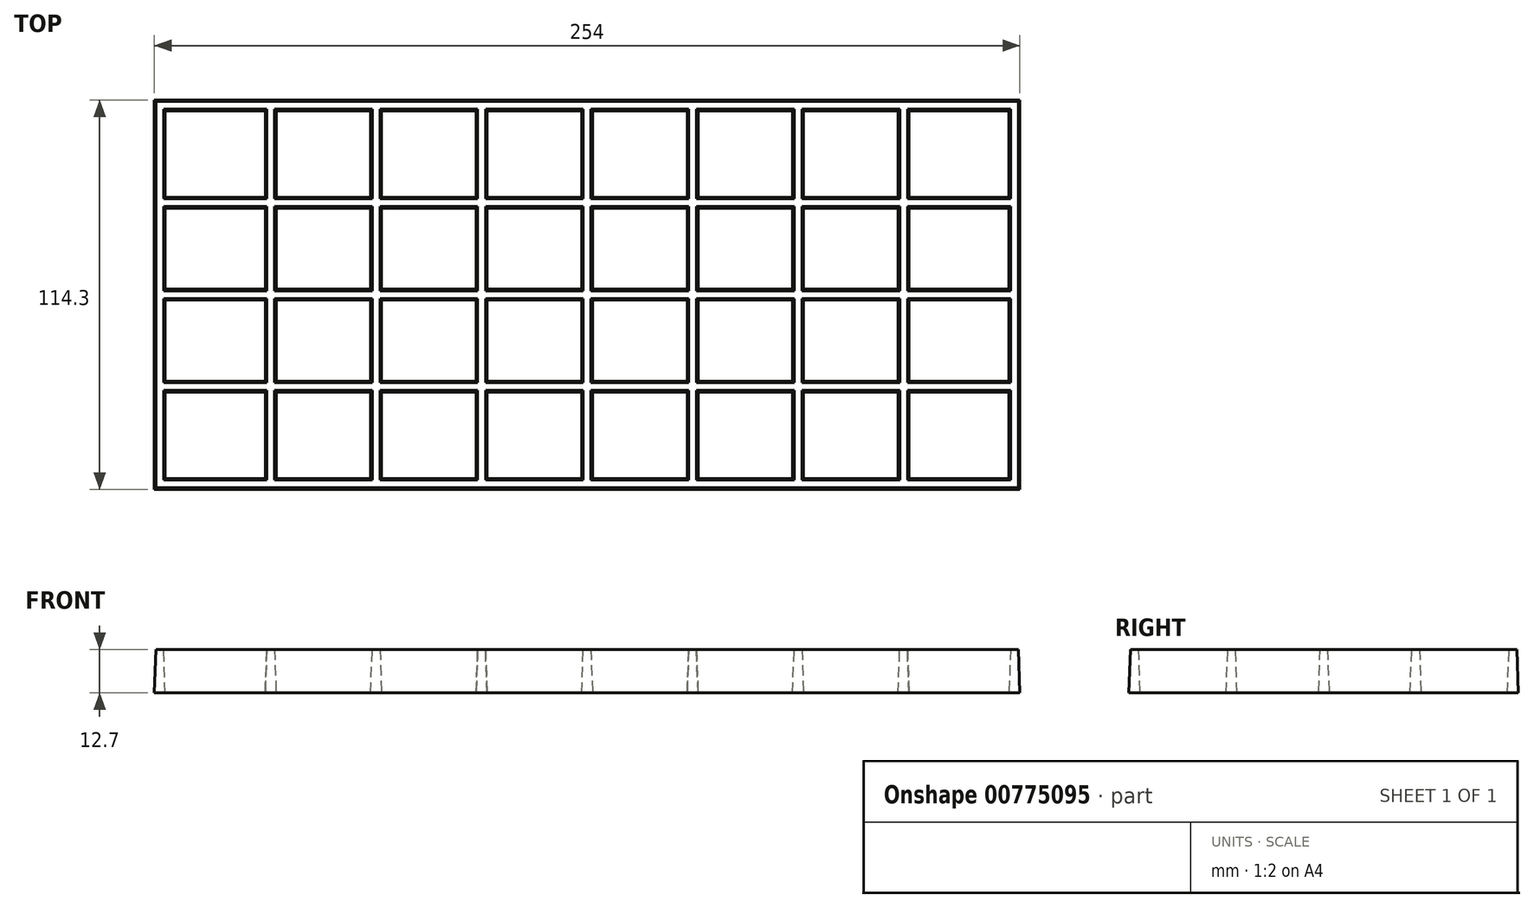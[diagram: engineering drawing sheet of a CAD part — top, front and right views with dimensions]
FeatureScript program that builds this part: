
annotation { "Feature Type Name" : "Feature", "Feature Type Description" : "" }
export const myFeature = defineFeature(function(context is Context, id is Id, definition is map)
    precondition{}
    {
        {
            var Q0;
            Q0=qCreatedBy(makeId("Top.planeOp"),FACE);
            var sketch = newSketch(context, id + "F0", { "sketchPlane" : qUnion([Q0])});
            skLineSegment(sketch, "E0.bottom", {"start": v(127, 57.15) * mm, "end": v(-127, 57.15) * mm});
            skLineSegment(sketch, "E0.top", {"start": v(127, -57.15) * mm, "end": v(-127, -57.15) * mm});
            skLineSegment(sketch, "E0.left", {"start": v(127, 57.15) * mm, "end": v(127, -57.15) * mm});
            skLineSegment(sketch, "E0.right", {"start": v(-127, 57.15) * mm, "end": v(-127, -57.15) * mm});
            skPoint(sketch, "E0.middle", {"position": v(0, 0) * mm});
            skLineSegment(sketch, "E1.0", {"start": v(123.82, 53.97) * mm, "end": v(-123.83, 53.98) * mm});
            skLineSegment(sketch, "E1.1", {"start": v(123.82, 53.97) * mm, "end": v(123.82, -53.97) * mm});
            skLineSegment(sketch, "E1.2", {"start": v(123.82, -53.98) * mm, "end": v(-123.83, -53.98) * mm});
            skLineSegment(sketch, "E1.3", {"start": v(-123.82, 53.98) * mm, "end": v(-123.83, -53.98) * mm});
            skLineSegment(sketch, "E2", {"start": v(-123.82, 26.99) * mm, "end": v(123.82, 26.99) * mm, "construction": true});
            skLineSegment(sketch, "E3", {"start": v(-123.83, 0) * mm, "end": v(123.82, 0) * mm, "construction": true});
            skLineSegment(sketch, "E4", {"start": v(-123.83, -26.99) * mm, "end": v(123.82, -26.99) * mm, "construction": true});
            skLineSegment(sketch, "E5", {"start": v(-92.87, 53.98) * mm, "end": v(-92.87, -53.98) * mm, "construction": true});
            skLineSegment(sketch, "E6", {"start": v(-61.91, 53.98) * mm, "end": v(-61.91, -53.98) * mm, "construction": true});
            skLineSegment(sketch, "E7", {"start": v(-30.96, 53.98) * mm, "end": v(-30.96, -53.98) * mm, "construction": true});
            skLineSegment(sketch, "E8", {"start": v(0, 53.98) * mm, "end": v(0, -53.98) * mm, "construction": true});
            skLineSegment(sketch, "E9", {"start": v(30.96, 53.98) * mm, "end": v(30.96, -53.98) * mm, "construction": true});
            skLineSegment(sketch, "E10", {"start": v(61.91, -53.98) * mm, "end": v(61.91, 53.98) * mm, "construction": true});
            skLineSegment(sketch, "E11", {"start": v(92.87, 53.97) * mm, "end": v(92.87, -53.97) * mm, "construction": true});
            skLineSegment(sketch, "E12.bottom", {"start": v(123.82, 28.58) * mm, "end": v(-123.82, 28.58) * mm});
            skLineSegment(sketch, "E12.top", {"start": v(123.82, 25.4) * mm, "end": v(-123.82, 25.4) * mm});
            skLineSegment(sketch, "E12.left", {"start": v(123.82, 28.58) * mm, "end": v(123.82, 25.4) * mm});
            skLineSegment(sketch, "E12.right", {"start": v(-123.82, 28.58) * mm, "end": v(-123.82, 25.4) * mm});
            skPoint(sketch, "E12.middle", {"position": v(0, 26.99) * mm});
            skLineSegment(sketch, "E13.bottom", {"start": v(123.82, 1.59) * mm, "end": v(-123.82, 1.59) * mm});
            skLineSegment(sketch, "E13.top", {"start": v(123.82, -1.59) * mm, "end": v(-123.82, -1.59) * mm});
            skLineSegment(sketch, "E13.left", {"start": v(123.82, 1.59) * mm, "end": v(123.82, -1.59) * mm});
            skLineSegment(sketch, "E13.right", {"start": v(-123.82, 1.59) * mm, "end": v(-123.82, -1.59) * mm});
            skLineSegment(sketch, "E14.bottom", {"start": v(123.82, -25.4) * mm, "end": v(-123.82, -25.4) * mm});
            skLineSegment(sketch, "E14.top", {"start": v(123.82, -28.57) * mm, "end": v(-123.82, -28.57) * mm});
            skLineSegment(sketch, "E14.left", {"start": v(123.82, -25.4) * mm, "end": v(123.82, -28.57) * mm});
            skLineSegment(sketch, "E14.right", {"start": v(-123.83, -25.4) * mm, "end": v(-123.83, -28.57) * mm});
            skPoint(sketch, "E14.middle", {"position": v(0, -26.99) * mm});
            skLineSegment(sketch, "E15.bottom", {"start": v(-91.28, 53.98) * mm, "end": v(-94.46, 53.98) * mm});
            skLineSegment(sketch, "E15.top", {"start": v(-91.28, -53.98) * mm, "end": v(-94.46, -53.98) * mm});
            skLineSegment(sketch, "E15.left", {"start": v(-91.28, 53.98) * mm, "end": v(-91.28, -53.98) * mm});
            skLineSegment(sketch, "E15.right", {"start": v(-94.46, 53.98) * mm, "end": v(-94.46, -53.98) * mm});
            skPoint(sketch, "E15.middle", {"position": v(-92.87, 0) * mm});
            skLineSegment(sketch, "E16.bottom", {"start": v(-60.32, 53.98) * mm, "end": v(-63.5, 53.98) * mm});
            skLineSegment(sketch, "E16.top", {"start": v(-60.32, -53.98) * mm, "end": v(-63.5, -53.98) * mm});
            skLineSegment(sketch, "E16.left", {"start": v(-60.32, 53.98) * mm, "end": v(-60.32, -53.98) * mm});
            skLineSegment(sketch, "E16.right", {"start": v(-63.5, 53.98) * mm, "end": v(-63.5, -53.98) * mm});
            skPoint(sketch, "E16.middle", {"position": v(-61.91, 0) * mm});
            skLineSegment(sketch, "E17.bottom", {"start": v(-29.37, 53.98) * mm, "end": v(-32.54, 53.98) * mm});
            skLineSegment(sketch, "E17.top", {"start": v(-29.37, -53.98) * mm, "end": v(-32.54, -53.98) * mm});
            skLineSegment(sketch, "E17.left", {"start": v(-29.37, 53.98) * mm, "end": v(-29.37, -53.98) * mm});
            skLineSegment(sketch, "E17.right", {"start": v(-32.54, 53.98) * mm, "end": v(-32.54, -53.98) * mm});
            skPoint(sketch, "E17.middle", {"position": v(-30.96, 0) * mm});
            skLineSegment(sketch, "E18.bottom", {"start": v(1.59, 53.98) * mm, "end": v(-1.59, 53.98) * mm});
            skLineSegment(sketch, "E18.top", {"start": v(1.59, -53.98) * mm, "end": v(-1.59, -53.98) * mm});
            skLineSegment(sketch, "E18.left", {"start": v(1.59, 53.98) * mm, "end": v(1.59, -53.98) * mm});
            skLineSegment(sketch, "E18.right", {"start": v(-1.59, 53.98) * mm, "end": v(-1.59, -53.98) * mm});
            skLineSegment(sketch, "E19.bottom", {"start": v(32.54, 53.98) * mm, "end": v(29.37, 53.98) * mm});
            skLineSegment(sketch, "E19.top", {"start": v(32.54, -53.98) * mm, "end": v(29.37, -53.98) * mm});
            skLineSegment(sketch, "E19.left", {"start": v(32.54, 53.98) * mm, "end": v(32.54, -53.98) * mm});
            skLineSegment(sketch, "E19.right", {"start": v(29.37, 53.98) * mm, "end": v(29.37, -53.98) * mm});
            skPoint(sketch, "E19.middle", {"position": v(30.96, 0) * mm});
            skLineSegment(sketch, "E20.bottom", {"start": v(63.5, 53.98) * mm, "end": v(60.33, 53.98) * mm});
            skLineSegment(sketch, "E20.top", {"start": v(63.5, -53.98) * mm, "end": v(60.33, -53.98) * mm});
            skLineSegment(sketch, "E20.left", {"start": v(63.5, 53.98) * mm, "end": v(63.5, -53.98) * mm});
            skLineSegment(sketch, "E20.right", {"start": v(60.33, 53.98) * mm, "end": v(60.33, -53.98) * mm});
            skPoint(sketch, "E20.middle", {"position": v(61.91, 0) * mm});
            skLineSegment(sketch, "E21.bottom", {"start": v(94.46, 53.97) * mm, "end": v(91.28, 53.97) * mm});
            skLineSegment(sketch, "E21.top", {"start": v(94.46, -53.97) * mm, "end": v(91.28, -53.97) * mm});
            skLineSegment(sketch, "E21.left", {"start": v(94.46, 53.98) * mm, "end": v(94.46, -53.98) * mm});
            skLineSegment(sketch, "E21.right", {"start": v(91.28, 53.98) * mm, "end": v(91.28, -53.98) * mm});
            skPoint(sketch, "E21.middle", {"position": v(92.87, 0) * mm});
            skSolve(sketch);
        }
        {
            var Q0;
            Q0=makeQuery(id+"F0.imprint","IMPRINT",FACE,{"disambiguationData":[TD([[makeQuery(id+"F0.imprint","IMPRINT",EDGE,{"derivedFrom":sQuery(id+"F0.wireOp",EDGE,"E0.bottom")}),1.0]])]});
            var Q1;
            {var subQ0=sQuery(id+"F0.wireOp",EDGE,"E15.right");var subQ1=sQuery(id+"F0.wireOp",EDGE,"E1.0");var subQ2=makeQuery(id+"F0.imprint","INTERSECT",VERTEX,{"derivedFrom":[subQ1,subQ0]});Q1=makeQuery(id+"F0.imprint","IMPRINT",FACE,{"disambiguationData":[TD([[makeQuery(id+"F0.imprint","IMPRINT",EDGE,{"disambiguationData":[TD([[subQ2,1.0]])],"derivedFrom":subQ1}),1.0]])]});}
            var Q2;
            {var subQ0=sQuery(id+"F0.wireOp",EDGE,"E16.right");var subQ1=sQuery(id+"F0.wireOp",EDGE,"E1.0");var subQ2=makeQuery(id+"F0.imprint","INTERSECT",VERTEX,{"derivedFrom":[subQ1,subQ0]});Q2=makeQuery(id+"F0.imprint","IMPRINT",FACE,{"disambiguationData":[TD([[makeQuery(id+"F0.imprint","IMPRINT",EDGE,{"disambiguationData":[TD([[subQ2,1.0]])],"derivedFrom":subQ1}),1.0]])]});}
            var Q3;
            {var subQ0=sQuery(id+"F0.wireOp",EDGE,"E17.right");var subQ1=sQuery(id+"F0.wireOp",EDGE,"E1.0");var subQ2=makeQuery(id+"F0.imprint","INTERSECT",VERTEX,{"derivedFrom":[subQ1,subQ0]});Q3=makeQuery(id+"F0.imprint","IMPRINT",FACE,{"disambiguationData":[TD([[makeQuery(id+"F0.imprint","IMPRINT",EDGE,{"disambiguationData":[TD([[subQ2,1.0]])],"derivedFrom":subQ1}),1.0]])]});}
            var Q4;
            {var subQ0=sQuery(id+"F0.wireOp",EDGE,"E18.left");var subQ1=sQuery(id+"F0.wireOp",EDGE,"E1.0");var subQ2=makeQuery(id+"F0.imprint","INTERSECT",VERTEX,{"derivedFrom":[subQ1,subQ0]});Q4=makeQuery(id+"F0.imprint","IMPRINT",FACE,{"disambiguationData":[TD([[makeQuery(id+"F0.imprint","IMPRINT",EDGE,{"disambiguationData":[TD([[subQ2,-1.0]])],"derivedFrom":subQ1}),1.0]])]});}
            var Q5;
            {var subQ0=sQuery(id+"F0.wireOp",EDGE,"E19.right");var subQ1=sQuery(id+"F0.wireOp",EDGE,"E1.0");var subQ2=makeQuery(id+"F0.imprint","INTERSECT",VERTEX,{"derivedFrom":[subQ1,subQ0]});Q5=makeQuery(id+"F0.imprint","IMPRINT",FACE,{"disambiguationData":[TD([[makeQuery(id+"F0.imprint","IMPRINT",EDGE,{"disambiguationData":[TD([[subQ2,1.0]])],"derivedFrom":subQ1}),1.0]])]});}
            var Q6;
            {var subQ0=sQuery(id+"F0.wireOp",EDGE,"E20.right");var subQ1=sQuery(id+"F0.wireOp",EDGE,"E1.0");var subQ2=makeQuery(id+"F0.imprint","INTERSECT",VERTEX,{"derivedFrom":[subQ1,subQ0]});Q6=makeQuery(id+"F0.imprint","IMPRINT",FACE,{"disambiguationData":[TD([[makeQuery(id+"F0.imprint","IMPRINT",EDGE,{"disambiguationData":[TD([[subQ2,1.0]])],"derivedFrom":subQ1}),1.0]])]});}
            var Q7;
            {var subQ0=sQuery(id+"F0.wireOp",EDGE,"E21.left");var subQ1=sQuery(id+"F0.wireOp",EDGE,"E1.0");var subQ2=makeQuery(id+"F0.imprint","INTERSECT",VERTEX,{"derivedFrom":[subQ1,subQ0]});Q7=makeQuery(id+"F0.imprint","IMPRINT",FACE,{"disambiguationData":[TD([[makeQuery(id+"F0.imprint","IMPRINT",EDGE,{"disambiguationData":[TD([[subQ2,-1.0]])],"derivedFrom":subQ1}),1.0]])]});}
            var Q8;
            {var subQ0=sQuery(id+"F0.wireOp",EDGE,"E12.top");var subQ1=sQuery(id+"F0.wireOp",EDGE,"E1.1");var subQ2=makeQuery(id+"F0.imprint","INTERSECT",VERTEX,{"derivedFrom":[subQ1,subQ0]});Q8=makeQuery(id+"F0.imprint","IMPRINT",FACE,{"disambiguationData":[TD([[makeQuery(id+"F0.imprint","IMPRINT",EDGE,{"disambiguationData":[TD([[subQ2,1.0]])],"derivedFrom":subQ1}),-1.0]])]});}
            var Q9;
            {var subQ0=sQuery(id+"F0.wireOp",EDGE,"E21.left");var subQ1=sQuery(id+"F0.wireOp",EDGE,"E12.bottom");var subQ2=makeQuery(id+"F0.imprint","INTERSECT",VERTEX,{"derivedFrom":[subQ1,subQ0]});Q9=makeQuery(id+"F0.imprint","IMPRINT",FACE,{"disambiguationData":[TD([[makeQuery(id+"F0.imprint","IMPRINT",EDGE,{"disambiguationData":[TD([[subQ2,-1.0]])],"derivedFrom":subQ1}),1.0]])]});}
            var Q10;
            {var subQ0=sQuery(id+"F0.wireOp",EDGE,"E21.right");var subQ1=sQuery(id+"F0.wireOp",EDGE,"E12.bottom");var subQ2=makeQuery(id+"F0.imprint","INTERSECT",VERTEX,{"derivedFrom":[subQ1,subQ0]});Q10=makeQuery(id+"F0.imprint","IMPRINT",FACE,{"disambiguationData":[TD([[makeQuery(id+"F0.imprint","IMPRINT",EDGE,{"disambiguationData":[TD([[subQ2,-1.0]])],"derivedFrom":subQ1}),1.0]])]});}
            var Q11;
            {var subQ0=sQuery(id+"F0.wireOp",EDGE,"E20.left");var subQ1=sQuery(id+"F0.wireOp",EDGE,"E12.bottom");var subQ2=makeQuery(id+"F0.imprint","INTERSECT",VERTEX,{"derivedFrom":[subQ1,subQ0]});Q11=makeQuery(id+"F0.imprint","IMPRINT",FACE,{"disambiguationData":[TD([[makeQuery(id+"F0.imprint","IMPRINT",EDGE,{"disambiguationData":[TD([[subQ2,-1.0]])],"derivedFrom":subQ1}),1.0]])]});}
            var Q12;
            {var subQ0=sQuery(id+"F0.wireOp",EDGE,"E19.right");var subQ1=sQuery(id+"F0.wireOp",EDGE,"E12.bottom");var subQ2=makeQuery(id+"F0.imprint","INTERSECT",VERTEX,{"derivedFrom":[subQ1,subQ0]});Q12=makeQuery(id+"F0.imprint","IMPRINT",FACE,{"disambiguationData":[TD([[makeQuery(id+"F0.imprint","IMPRINT",EDGE,{"disambiguationData":[TD([[subQ2,1.0]])],"derivedFrom":subQ1}),1.0]])]});}
            var Q13;
            {var subQ0=sQuery(id+"F0.wireOp",EDGE,"E19.left");var subQ1=sQuery(id+"F0.wireOp",EDGE,"E12.bottom");var subQ2=makeQuery(id+"F0.imprint","INTERSECT",VERTEX,{"derivedFrom":[subQ1,subQ0]});Q13=makeQuery(id+"F0.imprint","IMPRINT",FACE,{"disambiguationData":[TD([[makeQuery(id+"F0.imprint","IMPRINT",EDGE,{"disambiguationData":[TD([[subQ2,1.0]])],"derivedFrom":subQ1}),1.0]])]});}
            var Q14;
            {var subQ0=sQuery(id+"F0.wireOp",EDGE,"E19.right");var subQ1=sQuery(id+"F0.wireOp",EDGE,"E12.bottom");var subQ2=makeQuery(id+"F0.imprint","INTERSECT",VERTEX,{"derivedFrom":[subQ1,subQ0]});Q14=makeQuery(id+"F0.imprint","IMPRINT",FACE,{"disambiguationData":[TD([[makeQuery(id+"F0.imprint","IMPRINT",EDGE,{"disambiguationData":[TD([[subQ2,-1.0]])],"derivedFrom":subQ1}),1.0]])]});}
            var Q15;
            {var subQ0=sQuery(id+"F0.wireOp",EDGE,"E18.left");var subQ1=sQuery(id+"F0.wireOp",EDGE,"E12.bottom");var subQ2=makeQuery(id+"F0.imprint","INTERSECT",VERTEX,{"derivedFrom":[subQ1,subQ0]});Q15=makeQuery(id+"F0.imprint","IMPRINT",FACE,{"disambiguationData":[TD([[makeQuery(id+"F0.imprint","IMPRINT",EDGE,{"disambiguationData":[TD([[subQ2,-1.0]])],"derivedFrom":subQ1}),1.0]])]});}
            var Q16;
            {var subQ0=sQuery(id+"F0.wireOp",EDGE,"E17.left");var subQ1=sQuery(id+"F0.wireOp",EDGE,"E12.bottom");var subQ2=makeQuery(id+"F0.imprint","INTERSECT",VERTEX,{"derivedFrom":[subQ1,subQ0]});Q16=makeQuery(id+"F0.imprint","IMPRINT",FACE,{"disambiguationData":[TD([[makeQuery(id+"F0.imprint","IMPRINT",EDGE,{"disambiguationData":[TD([[subQ2,1.0]])],"derivedFrom":subQ1}),1.0]])]});}
            var Q17;
            {var subQ0=sQuery(id+"F0.wireOp",EDGE,"E17.right");var subQ1=sQuery(id+"F0.wireOp",EDGE,"E12.bottom");var subQ2=makeQuery(id+"F0.imprint","INTERSECT",VERTEX,{"derivedFrom":[subQ1,subQ0]});Q17=makeQuery(id+"F0.imprint","IMPRINT",FACE,{"disambiguationData":[TD([[makeQuery(id+"F0.imprint","IMPRINT",EDGE,{"disambiguationData":[TD([[subQ2,1.0]])],"derivedFrom":subQ1}),1.0]])]});}
            var Q18;
            {var subQ0=sQuery(id+"F0.wireOp",EDGE,"E17.right");var subQ1=sQuery(id+"F0.wireOp",EDGE,"E12.bottom");var subQ2=makeQuery(id+"F0.imprint","INTERSECT",VERTEX,{"derivedFrom":[subQ1,subQ0]});Q18=makeQuery(id+"F0.imprint","IMPRINT",FACE,{"disambiguationData":[TD([[makeQuery(id+"F0.imprint","IMPRINT",EDGE,{"disambiguationData":[TD([[subQ2,-1.0]])],"derivedFrom":subQ1}),1.0]])]});}
            var Q19;
            {var subQ0=sQuery(id+"F0.wireOp",EDGE,"E16.right");var subQ1=sQuery(id+"F0.wireOp",EDGE,"E12.bottom");var subQ2=makeQuery(id+"F0.imprint","INTERSECT",VERTEX,{"derivedFrom":[subQ1,subQ0]});Q19=makeQuery(id+"F0.imprint","IMPRINT",FACE,{"disambiguationData":[TD([[makeQuery(id+"F0.imprint","IMPRINT",EDGE,{"disambiguationData":[TD([[subQ2,1.0]])],"derivedFrom":subQ1}),1.0]])]});}
            var Q20;
            {var subQ0=sQuery(id+"F0.wireOp",EDGE,"E16.right");var subQ1=sQuery(id+"F0.wireOp",EDGE,"E12.bottom");var subQ2=makeQuery(id+"F0.imprint","INTERSECT",VERTEX,{"derivedFrom":[subQ1,subQ0]});Q20=makeQuery(id+"F0.imprint","IMPRINT",FACE,{"disambiguationData":[TD([[makeQuery(id+"F0.imprint","IMPRINT",EDGE,{"disambiguationData":[TD([[subQ2,-1.0]])],"derivedFrom":subQ1}),1.0]])]});}
            var Q21;
            {var subQ0=sQuery(id+"F0.wireOp",EDGE,"E15.right");var subQ1=sQuery(id+"F0.wireOp",EDGE,"E12.bottom");var subQ2=makeQuery(id+"F0.imprint","INTERSECT",VERTEX,{"derivedFrom":[subQ1,subQ0]});Q21=makeQuery(id+"F0.imprint","IMPRINT",FACE,{"disambiguationData":[TD([[makeQuery(id+"F0.imprint","IMPRINT",EDGE,{"disambiguationData":[TD([[subQ2,1.0]])],"derivedFrom":subQ1}),1.0]])]});}
            var Q22;
            {var subQ0=sQuery(id+"F0.wireOp",EDGE,"E12.top");var subQ1=sQuery(id+"F0.wireOp",EDGE,"E1.3");var subQ2=makeQuery(id+"F0.imprint","INTERSECT",VERTEX,{"derivedFrom":[subQ1,subQ0]});Q22=makeQuery(id+"F0.imprint","IMPRINT",FACE,{"disambiguationData":[TD([[makeQuery(id+"F0.imprint","IMPRINT",EDGE,{"disambiguationData":[TD([[subQ2,1.0]])],"derivedFrom":subQ1}),1.0]])]});}
            var Q23;
            {var subQ0=sQuery(id+"F0.wireOp",EDGE,"E15.right");var subQ1=sQuery(id+"F0.wireOp",EDGE,"E12.top");var subQ2=makeQuery(id+"F0.imprint","INTERSECT",VERTEX,{"derivedFrom":[subQ1,subQ0]});Q23=makeQuery(id+"F0.imprint","IMPRINT",FACE,{"disambiguationData":[TD([[makeQuery(id+"F0.imprint","IMPRINT",EDGE,{"disambiguationData":[TD([[subQ2,1.0]])],"derivedFrom":subQ1}),1.0]])]});}
            var Q24;
            {var subQ0=sQuery(id+"F0.wireOp",EDGE,"E16.left");var subQ1=sQuery(id+"F0.wireOp",EDGE,"E12.top");var subQ2=makeQuery(id+"F0.imprint","INTERSECT",VERTEX,{"derivedFrom":[subQ1,subQ0]});Q24=makeQuery(id+"F0.imprint","IMPRINT",FACE,{"disambiguationData":[TD([[makeQuery(id+"F0.imprint","IMPRINT",EDGE,{"disambiguationData":[TD([[subQ2,-1.0]])],"derivedFrom":subQ1}),1.0]])]});}
            var Q25;
            {var subQ0=sQuery(id+"F0.wireOp",EDGE,"E17.right");var subQ1=sQuery(id+"F0.wireOp",EDGE,"E12.top");var subQ2=makeQuery(id+"F0.imprint","INTERSECT",VERTEX,{"derivedFrom":[subQ1,subQ0]});Q25=makeQuery(id+"F0.imprint","IMPRINT",FACE,{"disambiguationData":[TD([[makeQuery(id+"F0.imprint","IMPRINT",EDGE,{"disambiguationData":[TD([[subQ2,1.0]])],"derivedFrom":subQ1}),1.0]])]});}
            var Q26;
            {var subQ0=sQuery(id+"F0.wireOp",EDGE,"E18.left");var subQ1=sQuery(id+"F0.wireOp",EDGE,"E12.top");var subQ2=makeQuery(id+"F0.imprint","INTERSECT",VERTEX,{"derivedFrom":[subQ1,subQ0]});Q26=makeQuery(id+"F0.imprint","IMPRINT",FACE,{"disambiguationData":[TD([[makeQuery(id+"F0.imprint","IMPRINT",EDGE,{"disambiguationData":[TD([[subQ2,-1.0]])],"derivedFrom":subQ1}),1.0]])]});}
            var Q27;
            {var subQ0=sQuery(id+"F0.wireOp",EDGE,"E19.right");var subQ1=sQuery(id+"F0.wireOp",EDGE,"E12.top");var subQ2=makeQuery(id+"F0.imprint","INTERSECT",VERTEX,{"derivedFrom":[subQ1,subQ0]});Q27=makeQuery(id+"F0.imprint","IMPRINT",FACE,{"disambiguationData":[TD([[makeQuery(id+"F0.imprint","IMPRINT",EDGE,{"disambiguationData":[TD([[subQ2,1.0]])],"derivedFrom":subQ1}),1.0]])]});}
            var Q28;
            {var subQ0=sQuery(id+"F0.wireOp",EDGE,"E20.right");var subQ1=sQuery(id+"F0.wireOp",EDGE,"E12.top");var subQ2=makeQuery(id+"F0.imprint","INTERSECT",VERTEX,{"derivedFrom":[subQ1,subQ0]});Q28=makeQuery(id+"F0.imprint","IMPRINT",FACE,{"disambiguationData":[TD([[makeQuery(id+"F0.imprint","IMPRINT",EDGE,{"disambiguationData":[TD([[subQ2,1.0]])],"derivedFrom":subQ1}),1.0]])]});}
            var Q29;
            {var subQ0=sQuery(id+"F0.wireOp",EDGE,"E21.right");var subQ1=sQuery(id+"F0.wireOp",EDGE,"E12.top");var subQ2=makeQuery(id+"F0.imprint","INTERSECT",VERTEX,{"derivedFrom":[subQ1,subQ0]});Q29=makeQuery(id+"F0.imprint","IMPRINT",FACE,{"disambiguationData":[TD([[makeQuery(id+"F0.imprint","IMPRINT",EDGE,{"disambiguationData":[TD([[subQ2,1.0]])],"derivedFrom":subQ1}),1.0]])]});}
            var Q30;
            {var subQ0=sQuery(id+"F0.wireOp",EDGE,"E21.left");var subQ1=sQuery(id+"F0.wireOp",EDGE,"E13.bottom");var subQ2=makeQuery(id+"F0.imprint","INTERSECT",VERTEX,{"derivedFrom":[subQ1,subQ0]});Q30=makeQuery(id+"F0.imprint","IMPRINT",FACE,{"disambiguationData":[TD([[makeQuery(id+"F0.imprint","IMPRINT",EDGE,{"disambiguationData":[TD([[subQ2,-1.0]])],"derivedFrom":subQ1}),1.0]])]});}
            var Q31;
            {var subQ0=sQuery(id+"F0.wireOp",EDGE,"E13.bottom");var subQ1=sQuery(id+"F0.wireOp",EDGE,"E1.1");var subQ2=makeQuery(id+"F0.imprint","INTERSECT",VERTEX,{"derivedFrom":[subQ1,subQ0]});Q31=makeQuery(id+"F0.imprint","IMPRINT",FACE,{"disambiguationData":[TD([[makeQuery(id+"F0.imprint","IMPRINT",EDGE,{"disambiguationData":[TD([[subQ2,-1.0]])],"derivedFrom":subQ1}),-1.0]])]});}
            var Q32;
            {var subQ0=sQuery(id+"F0.wireOp",EDGE,"E21.left");var subQ1=sQuery(id+"F0.wireOp",EDGE,"E13.top");var subQ2=makeQuery(id+"F0.imprint","INTERSECT",VERTEX,{"derivedFrom":[subQ1,subQ0]});Q32=makeQuery(id+"F0.imprint","IMPRINT",FACE,{"disambiguationData":[TD([[makeQuery(id+"F0.imprint","IMPRINT",EDGE,{"disambiguationData":[TD([[subQ2,-1.0]])],"derivedFrom":subQ1}),1.0]])]});}
            var Q33;
            {var subQ0=sQuery(id+"F0.wireOp",EDGE,"E21.right");var subQ1=sQuery(id+"F0.wireOp",EDGE,"E13.bottom");var subQ2=makeQuery(id+"F0.imprint","INTERSECT",VERTEX,{"derivedFrom":[subQ1,subQ0]});Q33=makeQuery(id+"F0.imprint","IMPRINT",FACE,{"disambiguationData":[TD([[makeQuery(id+"F0.imprint","IMPRINT",EDGE,{"disambiguationData":[TD([[subQ2,-1.0]])],"derivedFrom":subQ1}),1.0]])]});}
            var Q34;
            {var subQ0=sQuery(id+"F0.wireOp",EDGE,"E20.left");var subQ1=sQuery(id+"F0.wireOp",EDGE,"E13.top");var subQ2=makeQuery(id+"F0.imprint","INTERSECT",VERTEX,{"derivedFrom":[subQ1,subQ0]});Q34=makeQuery(id+"F0.imprint","IMPRINT",FACE,{"disambiguationData":[TD([[makeQuery(id+"F0.imprint","IMPRINT",EDGE,{"disambiguationData":[TD([[subQ2,-1.0]])],"derivedFrom":subQ1}),1.0]])]});}
            var Q35;
            {var subQ0=sQuery(id+"F0.wireOp",EDGE,"E20.right");var subQ1=sQuery(id+"F0.wireOp",EDGE,"E13.bottom");var subQ2=makeQuery(id+"F0.imprint","INTERSECT",VERTEX,{"derivedFrom":[subQ1,subQ0]});Q35=makeQuery(id+"F0.imprint","IMPRINT",FACE,{"disambiguationData":[TD([[makeQuery(id+"F0.imprint","IMPRINT",EDGE,{"disambiguationData":[TD([[subQ2,1.0]])],"derivedFrom":subQ1}),1.0]])]});}
            var Q36;
            {var subQ0=sQuery(id+"F0.wireOp",EDGE,"E20.right");var subQ1=sQuery(id+"F0.wireOp",EDGE,"E13.bottom");var subQ2=makeQuery(id+"F0.imprint","INTERSECT",VERTEX,{"derivedFrom":[subQ1,subQ0]});Q36=makeQuery(id+"F0.imprint","IMPRINT",FACE,{"disambiguationData":[TD([[makeQuery(id+"F0.imprint","IMPRINT",EDGE,{"disambiguationData":[TD([[subQ2,-1.0]])],"derivedFrom":subQ1}),1.0]])]});}
            var Q37;
            {var subQ0=sQuery(id+"F0.wireOp",EDGE,"E19.right");var subQ1=sQuery(id+"F0.wireOp",EDGE,"E13.bottom");var subQ2=makeQuery(id+"F0.imprint","INTERSECT",VERTEX,{"derivedFrom":[subQ1,subQ0]});Q37=makeQuery(id+"F0.imprint","IMPRINT",FACE,{"disambiguationData":[TD([[makeQuery(id+"F0.imprint","IMPRINT",EDGE,{"disambiguationData":[TD([[subQ2,1.0]])],"derivedFrom":subQ1}),1.0]])]});}
            var Q38;
            {var subQ0=sQuery(id+"F0.wireOp",EDGE,"E18.left");var subQ1=sQuery(id+"F0.wireOp",EDGE,"E13.bottom");var subQ2=makeQuery(id+"F0.imprint","INTERSECT",VERTEX,{"derivedFrom":[subQ1,subQ0]});Q38=makeQuery(id+"F0.imprint","IMPRINT",FACE,{"disambiguationData":[TD([[makeQuery(id+"F0.imprint","IMPRINT",EDGE,{"disambiguationData":[TD([[subQ2,1.0]])],"derivedFrom":subQ1}),1.0]])]});}
            var Q39;
            {var subQ0=sQuery(id+"F0.wireOp",EDGE,"E17.right");var subQ1=sQuery(id+"F0.wireOp",EDGE,"E13.bottom");var subQ2=makeQuery(id+"F0.imprint","INTERSECT",VERTEX,{"derivedFrom":[subQ1,subQ0]});Q39=makeQuery(id+"F0.imprint","IMPRINT",FACE,{"disambiguationData":[TD([[makeQuery(id+"F0.imprint","IMPRINT",EDGE,{"disambiguationData":[TD([[subQ2,-1.0]])],"derivedFrom":subQ1}),1.0]])]});}
            var Q40;
            {var subQ0=sQuery(id+"F0.wireOp",EDGE,"E16.right");var subQ1=sQuery(id+"F0.wireOp",EDGE,"E13.bottom");var subQ2=makeQuery(id+"F0.imprint","INTERSECT",VERTEX,{"derivedFrom":[subQ1,subQ0]});Q40=makeQuery(id+"F0.imprint","IMPRINT",FACE,{"disambiguationData":[TD([[makeQuery(id+"F0.imprint","IMPRINT",EDGE,{"disambiguationData":[TD([[subQ2,1.0]])],"derivedFrom":subQ1}),1.0]])]});}
            var Q41;
            {var subQ0=sQuery(id+"F0.wireOp",EDGE,"E16.right");var subQ1=sQuery(id+"F0.wireOp",EDGE,"E13.bottom");var subQ2=makeQuery(id+"F0.imprint","INTERSECT",VERTEX,{"derivedFrom":[subQ1,subQ0]});Q41=makeQuery(id+"F0.imprint","IMPRINT",FACE,{"disambiguationData":[TD([[makeQuery(id+"F0.imprint","IMPRINT",EDGE,{"disambiguationData":[TD([[subQ2,-1.0]])],"derivedFrom":subQ1}),1.0]])]});}
            var Q42;
            {var subQ0=sQuery(id+"F0.wireOp",EDGE,"E13.bottom");var subQ1=sQuery(id+"F0.wireOp",EDGE,"E1.3");var subQ2=makeQuery(id+"F0.imprint","INTERSECT",VERTEX,{"derivedFrom":[subQ1,subQ0]});Q42=makeQuery(id+"F0.imprint","IMPRINT",FACE,{"disambiguationData":[TD([[makeQuery(id+"F0.imprint","IMPRINT",EDGE,{"disambiguationData":[TD([[subQ2,-1.0]])],"derivedFrom":subQ1}),1.0]])]});}
            var Q43;
            {var subQ0=sQuery(id+"F0.wireOp",EDGE,"E15.right");var subQ1=sQuery(id+"F0.wireOp",EDGE,"E13.bottom");var subQ2=makeQuery(id+"F0.imprint","INTERSECT",VERTEX,{"derivedFrom":[subQ1,subQ0]});Q43=makeQuery(id+"F0.imprint","IMPRINT",FACE,{"disambiguationData":[TD([[makeQuery(id+"F0.imprint","IMPRINT",EDGE,{"disambiguationData":[TD([[subQ2,1.0]])],"derivedFrom":subQ1}),1.0]])]});}
            var Q44;
            {var subQ0=sQuery(id+"F0.wireOp",EDGE,"E17.left");var subQ1=sQuery(id+"F0.wireOp",EDGE,"E13.bottom");var subQ2=makeQuery(id+"F0.imprint","INTERSECT",VERTEX,{"derivedFrom":[subQ1,subQ0]});Q44=makeQuery(id+"F0.imprint","IMPRINT",FACE,{"disambiguationData":[TD([[makeQuery(id+"F0.imprint","IMPRINT",EDGE,{"disambiguationData":[TD([[subQ2,1.0]])],"derivedFrom":subQ1}),1.0]])]});}
            var Q45;
            {var subQ0=sQuery(id+"F0.wireOp",EDGE,"E17.right");var subQ1=sQuery(id+"F0.wireOp",EDGE,"E13.bottom");var subQ2=makeQuery(id+"F0.imprint","INTERSECT",VERTEX,{"derivedFrom":[subQ1,subQ0]});Q45=makeQuery(id+"F0.imprint","IMPRINT",FACE,{"disambiguationData":[TD([[makeQuery(id+"F0.imprint","IMPRINT",EDGE,{"disambiguationData":[TD([[subQ2,1.0]])],"derivedFrom":subQ1}),1.0]])]});}
            var Q46;
            {var subQ0=sQuery(id+"F0.wireOp",EDGE,"E15.right");var subQ1=sQuery(id+"F0.wireOp",EDGE,"E13.top");var subQ2=makeQuery(id+"F0.imprint","INTERSECT",VERTEX,{"derivedFrom":[subQ1,subQ0]});Q46=makeQuery(id+"F0.imprint","IMPRINT",FACE,{"disambiguationData":[TD([[makeQuery(id+"F0.imprint","IMPRINT",EDGE,{"disambiguationData":[TD([[subQ2,1.0]])],"derivedFrom":subQ1}),1.0]])]});}
            var Q47;
            {var subQ0=sQuery(id+"F0.wireOp",EDGE,"E16.left");var subQ1=sQuery(id+"F0.wireOp",EDGE,"E13.top");var subQ2=makeQuery(id+"F0.imprint","INTERSECT",VERTEX,{"derivedFrom":[subQ1,subQ0]});Q47=makeQuery(id+"F0.imprint","IMPRINT",FACE,{"disambiguationData":[TD([[makeQuery(id+"F0.imprint","IMPRINT",EDGE,{"disambiguationData":[TD([[subQ2,-1.0]])],"derivedFrom":subQ1}),1.0]])]});}
            var Q48;
            {var subQ0=sQuery(id+"F0.wireOp",EDGE,"E17.right");var subQ1=sQuery(id+"F0.wireOp",EDGE,"E13.top");var subQ2=makeQuery(id+"F0.imprint","INTERSECT",VERTEX,{"derivedFrom":[subQ1,subQ0]});Q48=makeQuery(id+"F0.imprint","IMPRINT",FACE,{"disambiguationData":[TD([[makeQuery(id+"F0.imprint","IMPRINT",EDGE,{"disambiguationData":[TD([[subQ2,1.0]])],"derivedFrom":subQ1}),1.0]])]});}
            var Q49;
            {var subQ0=sQuery(id+"F0.wireOp",EDGE,"E18.left");var subQ1=sQuery(id+"F0.wireOp",EDGE,"E13.top");var subQ2=makeQuery(id+"F0.imprint","INTERSECT",VERTEX,{"derivedFrom":[subQ1,subQ0]});Q49=makeQuery(id+"F0.imprint","IMPRINT",FACE,{"disambiguationData":[TD([[makeQuery(id+"F0.imprint","IMPRINT",EDGE,{"disambiguationData":[TD([[subQ2,-1.0]])],"derivedFrom":subQ1}),1.0]])]});}
            var Q50;
            {var subQ0=sQuery(id+"F0.wireOp",EDGE,"E19.right");var subQ1=sQuery(id+"F0.wireOp",EDGE,"E13.top");var subQ2=makeQuery(id+"F0.imprint","INTERSECT",VERTEX,{"derivedFrom":[subQ1,subQ0]});Q50=makeQuery(id+"F0.imprint","IMPRINT",FACE,{"disambiguationData":[TD([[makeQuery(id+"F0.imprint","IMPRINT",EDGE,{"disambiguationData":[TD([[subQ2,1.0]])],"derivedFrom":subQ1}),1.0]])]});}
            var Q51;
            {var subQ0=sQuery(id+"F0.wireOp",EDGE,"E14.top");var subQ1=sQuery(id+"F0.wireOp",EDGE,"E1.1");var subQ2=makeQuery(id+"F0.imprint","INTERSECT",VERTEX,{"derivedFrom":[subQ1,subQ0]});Q51=makeQuery(id+"F0.imprint","IMPRINT",FACE,{"disambiguationData":[TD([[makeQuery(id+"F0.imprint","IMPRINT",EDGE,{"disambiguationData":[TD([[subQ2,1.0]])],"derivedFrom":subQ1}),-1.0]])]});}
            var Q52;
            {var subQ0=sQuery(id+"F0.wireOp",EDGE,"E21.left");var subQ1=sQuery(id+"F0.wireOp",EDGE,"E14.bottom");var subQ2=makeQuery(id+"F0.imprint","INTERSECT",VERTEX,{"derivedFrom":[subQ1,subQ0]});Q52=makeQuery(id+"F0.imprint","IMPRINT",FACE,{"disambiguationData":[TD([[makeQuery(id+"F0.imprint","IMPRINT",EDGE,{"disambiguationData":[TD([[subQ2,-1.0]])],"derivedFrom":subQ1}),1.0]])]});}
            var Q53;
            {var subQ0=sQuery(id+"F0.wireOp",EDGE,"E21.right");var subQ1=sQuery(id+"F0.wireOp",EDGE,"E14.bottom");var subQ2=makeQuery(id+"F0.imprint","INTERSECT",VERTEX,{"derivedFrom":[subQ1,subQ0]});Q53=makeQuery(id+"F0.imprint","IMPRINT",FACE,{"disambiguationData":[TD([[makeQuery(id+"F0.imprint","IMPRINT",EDGE,{"disambiguationData":[TD([[subQ2,-1.0]])],"derivedFrom":subQ1}),1.0]])]});}
            var Q54;
            {var subQ0=sQuery(id+"F0.wireOp",EDGE,"E20.left");var subQ1=sQuery(id+"F0.wireOp",EDGE,"E14.bottom");var subQ2=makeQuery(id+"F0.imprint","INTERSECT",VERTEX,{"derivedFrom":[subQ1,subQ0]});Q54=makeQuery(id+"F0.imprint","IMPRINT",FACE,{"disambiguationData":[TD([[makeQuery(id+"F0.imprint","IMPRINT",EDGE,{"disambiguationData":[TD([[subQ2,-1.0]])],"derivedFrom":subQ1}),1.0]])]});}
            var Q55;
            {var subQ0=sQuery(id+"F0.wireOp",EDGE,"E20.right");var subQ1=sQuery(id+"F0.wireOp",EDGE,"E14.bottom");var subQ2=makeQuery(id+"F0.imprint","INTERSECT",VERTEX,{"derivedFrom":[subQ1,subQ0]});Q55=makeQuery(id+"F0.imprint","IMPRINT",FACE,{"disambiguationData":[TD([[makeQuery(id+"F0.imprint","IMPRINT",EDGE,{"disambiguationData":[TD([[subQ2,-1.0]])],"derivedFrom":subQ1}),1.0]])]});}
            var Q56;
            {var subQ0=sQuery(id+"F0.wireOp",EDGE,"E19.right");var subQ1=sQuery(id+"F0.wireOp",EDGE,"E14.bottom");var subQ2=makeQuery(id+"F0.imprint","INTERSECT",VERTEX,{"derivedFrom":[subQ1,subQ0]});Q56=makeQuery(id+"F0.imprint","IMPRINT",FACE,{"disambiguationData":[TD([[makeQuery(id+"F0.imprint","IMPRINT",EDGE,{"disambiguationData":[TD([[subQ2,1.0]])],"derivedFrom":subQ1}),1.0]])]});}
            var Q57;
            {var subQ0=sQuery(id+"F0.wireOp",EDGE,"E19.right");var subQ1=sQuery(id+"F0.wireOp",EDGE,"E14.bottom");var subQ2=makeQuery(id+"F0.imprint","INTERSECT",VERTEX,{"derivedFrom":[subQ1,subQ0]});Q57=makeQuery(id+"F0.imprint","IMPRINT",FACE,{"disambiguationData":[TD([[makeQuery(id+"F0.imprint","IMPRINT",EDGE,{"disambiguationData":[TD([[subQ2,-1.0]])],"derivedFrom":subQ1}),1.0]])]});}
            var Q58;
            {var subQ0=sQuery(id+"F0.wireOp",EDGE,"E18.left");var subQ1=sQuery(id+"F0.wireOp",EDGE,"E14.bottom");var subQ2=makeQuery(id+"F0.imprint","INTERSECT",VERTEX,{"derivedFrom":[subQ1,subQ0]});Q58=makeQuery(id+"F0.imprint","IMPRINT",FACE,{"disambiguationData":[TD([[makeQuery(id+"F0.imprint","IMPRINT",EDGE,{"disambiguationData":[TD([[subQ2,-1.0]])],"derivedFrom":subQ1}),1.0]])]});}
            var Q59;
            {var subQ0=sQuery(id+"F0.wireOp",EDGE,"E17.left");var subQ1=sQuery(id+"F0.wireOp",EDGE,"E14.bottom");var subQ2=makeQuery(id+"F0.imprint","INTERSECT",VERTEX,{"derivedFrom":[subQ1,subQ0]});Q59=makeQuery(id+"F0.imprint","IMPRINT",FACE,{"disambiguationData":[TD([[makeQuery(id+"F0.imprint","IMPRINT",EDGE,{"disambiguationData":[TD([[subQ2,1.0]])],"derivedFrom":subQ1}),1.0]])]});}
            var Q60;
            {var subQ0=sQuery(id+"F0.wireOp",EDGE,"E17.right");var subQ1=sQuery(id+"F0.wireOp",EDGE,"E14.bottom");var subQ2=makeQuery(id+"F0.imprint","INTERSECT",VERTEX,{"derivedFrom":[subQ1,subQ0]});Q60=makeQuery(id+"F0.imprint","IMPRINT",FACE,{"disambiguationData":[TD([[makeQuery(id+"F0.imprint","IMPRINT",EDGE,{"disambiguationData":[TD([[subQ2,1.0]])],"derivedFrom":subQ1}),1.0]])]});}
            var Q61;
            {var subQ0=sQuery(id+"F0.wireOp",EDGE,"E17.right");var subQ1=sQuery(id+"F0.wireOp",EDGE,"E14.bottom");var subQ2=makeQuery(id+"F0.imprint","INTERSECT",VERTEX,{"derivedFrom":[subQ1,subQ0]});Q61=makeQuery(id+"F0.imprint","IMPRINT",FACE,{"disambiguationData":[TD([[makeQuery(id+"F0.imprint","IMPRINT",EDGE,{"disambiguationData":[TD([[subQ2,-1.0]])],"derivedFrom":subQ1}),1.0]])]});}
            var Q62;
            {var subQ0=sQuery(id+"F0.wireOp",EDGE,"E16.left");var subQ1=sQuery(id+"F0.wireOp",EDGE,"E14.bottom");var subQ2=makeQuery(id+"F0.imprint","INTERSECT",VERTEX,{"derivedFrom":[subQ1,subQ0]});Q62=makeQuery(id+"F0.imprint","IMPRINT",FACE,{"disambiguationData":[TD([[makeQuery(id+"F0.imprint","IMPRINT",EDGE,{"disambiguationData":[TD([[subQ2,-1.0]])],"derivedFrom":subQ1}),1.0]])]});}
            var Q63;
            {var subQ0=sQuery(id+"F0.wireOp",EDGE,"E16.right");var subQ1=sQuery(id+"F0.wireOp",EDGE,"E14.bottom");var subQ2=makeQuery(id+"F0.imprint","INTERSECT",VERTEX,{"derivedFrom":[subQ1,subQ0]});Q63=makeQuery(id+"F0.imprint","IMPRINT",FACE,{"disambiguationData":[TD([[makeQuery(id+"F0.imprint","IMPRINT",EDGE,{"disambiguationData":[TD([[subQ2,-1.0]])],"derivedFrom":subQ1}),1.0]])]});}
            var Q64;
            {var subQ0=sQuery(id+"F0.wireOp",EDGE,"E15.right");var subQ1=sQuery(id+"F0.wireOp",EDGE,"E14.bottom");var subQ2=makeQuery(id+"F0.imprint","INTERSECT",VERTEX,{"derivedFrom":[subQ1,subQ0]});Q64=makeQuery(id+"F0.imprint","IMPRINT",FACE,{"disambiguationData":[TD([[makeQuery(id+"F0.imprint","IMPRINT",EDGE,{"disambiguationData":[TD([[subQ2,1.0]])],"derivedFrom":subQ1}),1.0]])]});}
            var Q65;
            {var subQ0=sQuery(id+"F0.wireOp",EDGE,"E14.top");var subQ1=sQuery(id+"F0.wireOp",EDGE,"E1.3");var subQ2=makeQuery(id+"F0.imprint","INTERSECT",VERTEX,{"derivedFrom":[subQ1,subQ0]});Q65=makeQuery(id+"F0.imprint","IMPRINT",FACE,{"disambiguationData":[TD([[makeQuery(id+"F0.imprint","IMPRINT",EDGE,{"disambiguationData":[TD([[subQ2,1.0]])],"derivedFrom":subQ1}),1.0]])]});}
            var Q66;
            {var subQ0=sQuery(id+"F0.wireOp",EDGE,"E15.right");var subQ1=sQuery(id+"F0.wireOp",EDGE,"E1.2");var subQ2=makeQuery(id+"F0.imprint","INTERSECT",VERTEX,{"derivedFrom":[subQ1,subQ0]});Q66=makeQuery(id+"F0.imprint","IMPRINT",FACE,{"disambiguationData":[TD([[makeQuery(id+"F0.imprint","IMPRINT",EDGE,{"disambiguationData":[TD([[subQ2,1.0]])],"derivedFrom":subQ1}),-1.0]])]});}
            var Q67;
            {var subQ0=sQuery(id+"F0.wireOp",EDGE,"E16.right");var subQ1=sQuery(id+"F0.wireOp",EDGE,"E1.2");var subQ2=makeQuery(id+"F0.imprint","INTERSECT",VERTEX,{"derivedFrom":[subQ1,subQ0]});Q67=makeQuery(id+"F0.imprint","IMPRINT",FACE,{"disambiguationData":[TD([[makeQuery(id+"F0.imprint","IMPRINT",EDGE,{"disambiguationData":[TD([[subQ2,1.0]])],"derivedFrom":subQ1}),-1.0]])]});}
            var Q68;
            {var subQ0=sQuery(id+"F0.wireOp",EDGE,"E17.right");var subQ1=sQuery(id+"F0.wireOp",EDGE,"E1.2");var subQ2=makeQuery(id+"F0.imprint","INTERSECT",VERTEX,{"derivedFrom":[subQ1,subQ0]});Q68=makeQuery(id+"F0.imprint","IMPRINT",FACE,{"disambiguationData":[TD([[makeQuery(id+"F0.imprint","IMPRINT",EDGE,{"disambiguationData":[TD([[subQ2,1.0]])],"derivedFrom":subQ1}),-1.0]])]});}
            var Q69;
            {var subQ0=sQuery(id+"F0.wireOp",EDGE,"E18.left");var subQ1=sQuery(id+"F0.wireOp",EDGE,"E1.2");var subQ2=makeQuery(id+"F0.imprint","INTERSECT",VERTEX,{"derivedFrom":[subQ1,subQ0]});Q69=makeQuery(id+"F0.imprint","IMPRINT",FACE,{"disambiguationData":[TD([[makeQuery(id+"F0.imprint","IMPRINT",EDGE,{"disambiguationData":[TD([[subQ2,-1.0]])],"derivedFrom":subQ1}),-1.0]])]});}
            var Q70;
            {var subQ0=sQuery(id+"F0.wireOp",EDGE,"E19.right");var subQ1=sQuery(id+"F0.wireOp",EDGE,"E1.2");var subQ2=makeQuery(id+"F0.imprint","INTERSECT",VERTEX,{"derivedFrom":[subQ1,subQ0]});Q70=makeQuery(id+"F0.imprint","IMPRINT",FACE,{"disambiguationData":[TD([[makeQuery(id+"F0.imprint","IMPRINT",EDGE,{"disambiguationData":[TD([[subQ2,1.0]])],"derivedFrom":subQ1}),-1.0]])]});}
            var Q71;
            {var subQ0=sQuery(id+"F0.wireOp",EDGE,"E20.right");var subQ1=sQuery(id+"F0.wireOp",EDGE,"E1.2");var subQ2=makeQuery(id+"F0.imprint","INTERSECT",VERTEX,{"derivedFrom":[subQ1,subQ0]});Q71=makeQuery(id+"F0.imprint","IMPRINT",FACE,{"disambiguationData":[TD([[makeQuery(id+"F0.imprint","IMPRINT",EDGE,{"disambiguationData":[TD([[subQ2,1.0]])],"derivedFrom":subQ1}),-1.0]])]});}
            var Q72;
            {var subQ0=sQuery(id+"F0.wireOp",EDGE,"E21.left");var subQ1=sQuery(id+"F0.wireOp",EDGE,"E1.2");var subQ2=makeQuery(id+"F0.imprint","INTERSECT",VERTEX,{"derivedFrom":[subQ1,subQ0]});Q72=makeQuery(id+"F0.imprint","IMPRINT",FACE,{"disambiguationData":[TD([[makeQuery(id+"F0.imprint","IMPRINT",EDGE,{"disambiguationData":[TD([[subQ2,-1.0]])],"derivedFrom":subQ1}),-1.0]])]});}
            var Q73;
            {var subQ0=sQuery(id+"F0.wireOp",EDGE,"E18.left");var subQ1=sQuery(id+"F0.wireOp",EDGE,"E13.bottom");var subQ2=makeQuery(id+"F0.imprint","INTERSECT",VERTEX,{"derivedFrom":[subQ1,subQ0]});Q73=makeQuery(id+"F0.imprint","IMPRINT",FACE,{"disambiguationData":[TD([[makeQuery(id+"F0.imprint","IMPRINT",EDGE,{"disambiguationData":[TD([[subQ2,-1.0]])],"derivedFrom":subQ1}),1.0]])]});}
            extrude(context, id + "F1", {"entities" : qUnion([Q0, Q1, Q2, Q3, Q4, Q5, Q6, Q7, Q8, Q9, Q10, Q11, Q12, Q13, Q14, Q15, Q16, Q17, Q18, Q19, Q20, Q21, Q22, Q23, Q24, Q25, Q26, Q27, Q28, Q29, Q30, Q31, Q32, Q33, Q34, Q35, Q36, Q37, Q38, Q39, Q40, Q41, Q42, Q43, Q44, Q45, Q46, Q47, Q48, Q49, Q50, Q51, Q52, Q53, Q54, Q55, Q56, Q57, Q58, Q59, Q60, Q61, Q62, Q63, Q64, Q65, Q66, Q67, Q68, Q69, Q70, Q71, Q72, Q73]), "depth" : 12.7 * mm, "offsetDistance" : 25.4 * mm, "hasDraft" : true, "draftAngle" : 2 * degree, "draftPullDirection" : true});
        }
    });
